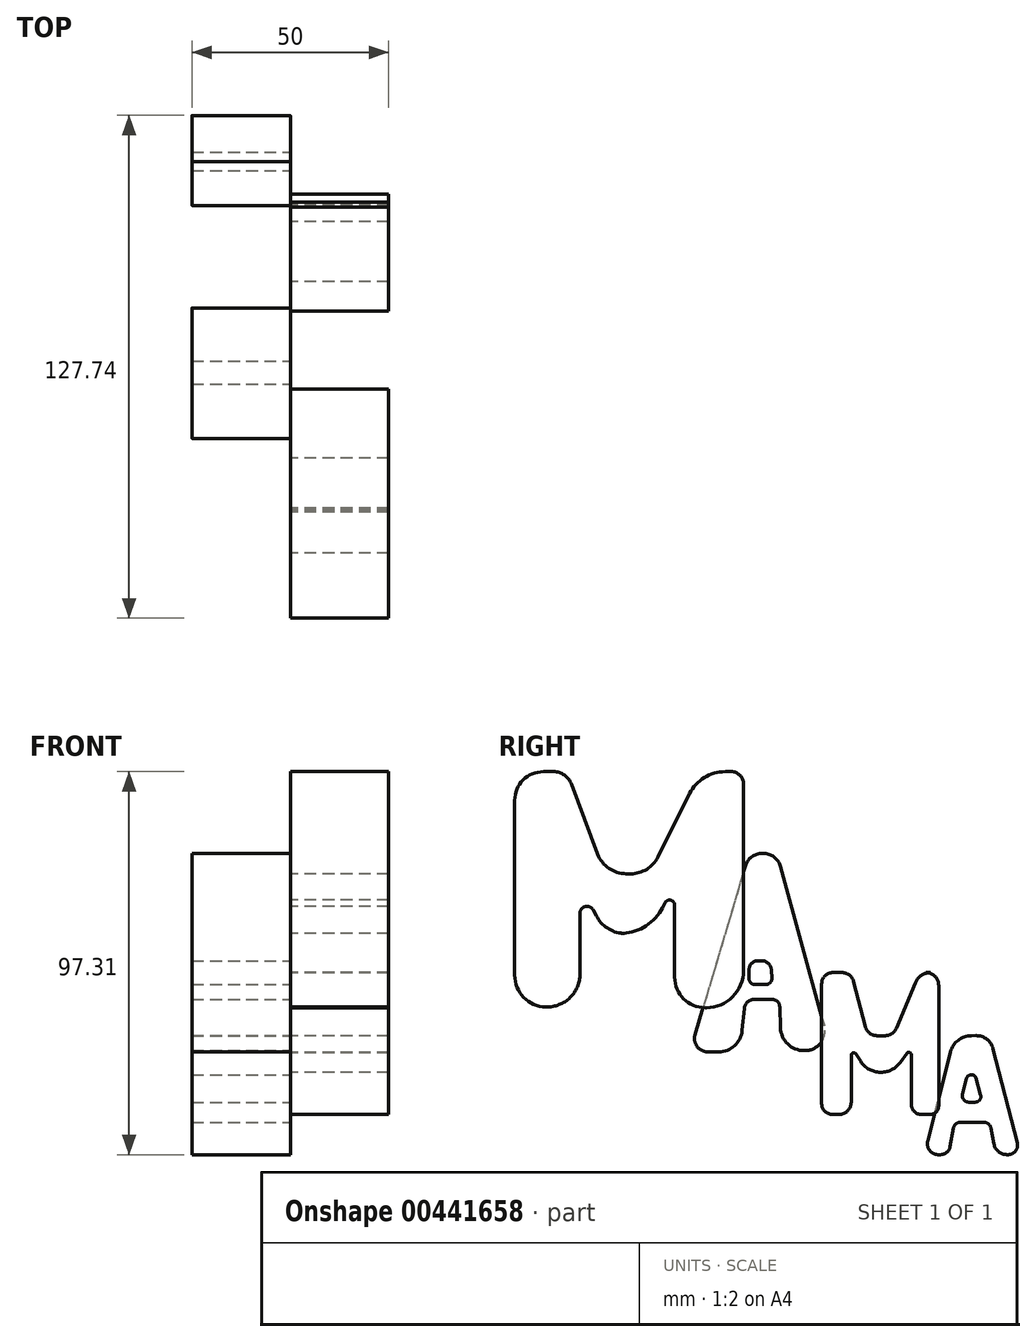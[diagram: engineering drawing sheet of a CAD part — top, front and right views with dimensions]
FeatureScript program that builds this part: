
annotation { "Feature Type Name" : "Feature", "Feature Type Description" : "" }
export const myFeature = defineFeature(function(context is Context, id is Id, definition is map)
    precondition{}
    {
        {
            var Q0;
            Q0=qCreatedBy(makeId("Right.planeOp"),FACE);
            var sketch = newSketch(context, id + "F0", { "sketchPlane" : qUnion([Q0])});
            skLineSegment(sketch, "E0", {"start": v(-70.27, 15.39) * mm, "end": v(-70.27, 59.77) * mm});
            skLineSegment(sketch, "E1", {"start": v(-62.96, 67.08) * mm, "end": v(-60.43, 67.08) * mm});
            skLineSegment(sketch, "E2", {"start": v(-55.84, 63.9) * mm, "end": v(-49.18, 46.14) * mm});
            skLineSegment(sketch, "E3", {"start": v(-41.96, 41.14) * mm, "end": v(-40.77, 41.14) * mm});
            skLineSegment(sketch, "E4", {"start": v(-33.87, 45.4) * mm, "end": v(-25.83, 61.5) * mm});
            skLineSegment(sketch, "E5", {"start": v(-16.78, 67.08) * mm, "end": v(-15.23, 67.08) * mm});
            skLineSegment(sketch, "E6", {"start": v(-12.12, 63.97) * mm, "end": v(-12.12, 16.58) * mm});
            skLineSegment(sketch, "E7", {"start": v(-21.6, 7.1) * mm, "end": v(-21.85, 7.1) * mm});
            skLineSegment(sketch, "E8", {"start": v(-29.62, 14.89) * mm, "end": v(-29.62, 33.15) * mm});
            skLineSegment(sketch, "E9", {"start": v(-32.1, 33.74) * mm, "end": v(-32.71, 32.52) * mm});
            skLineSegment(sketch, "E10", {"start": v(-42.31, 26) * mm, "end": v(-43.3, 26) * mm});
            skLineSegment(sketch, "E11", {"start": v(-49.56, 30.46) * mm, "end": v(-50.27, 31.88) * mm});
            skLineSegment(sketch, "E12", {"start": v(-53.68, 31.07) * mm, "end": v(-53.68, 15.69) * mm});
            skLineSegment(sketch, "E13", {"start": v(-62.26, 7.3) * mm, "end": v(-62.36, 7.3) * mm});
            skPoint(sketch, "E14.visualSharp", {"position": v(-70.27, 67.08) * mm});
            skArc(sketch, "E14.filletArc", {"start": v(-62.96, 67.08) * mm, "mid": v(-68.13, 64.94) * mm, "end": v(-70.27, 59.77) * mm});
            skPoint(sketch, "E15.visualSharp", {"position": v(-57.03, 67.08) * mm});
            skArc(sketch, "E15.filletArc", {"start": v(-55.84, 63.9) * mm, "mid": v(-57.64, 66.21) * mm, "end": v(-60.43, 67.08) * mm});
            skPoint(sketch, "E16.visualSharp", {"position": v(-23.03, 67.08) * mm});
            skArc(sketch, "E16.filletArc", {"start": v(-16.78, 67.08) * mm, "mid": v(-22.1, 65.57) * mm, "end": v(-25.83, 61.5) * mm});
            skPoint(sketch, "E17.visualSharp", {"position": v(-12.12, 67.08) * mm});
            skArc(sketch, "E17.filletArc", {"start": v(-12.12, 63.97) * mm, "mid": v(-13.03, 66.17) * mm, "end": v(-15.23, 67.08) * mm});
            skPoint(sketch, "E18.visualSharp", {"position": v(-12.12, 7.1) * mm});
            skArc(sketch, "E18.filletArc", {"start": v(-21.6, 7.1) * mm, "mid": v(-14.9, 9.88) * mm, "end": v(-12.12, 16.58) * mm});
            skPoint(sketch, "E19.visualSharp", {"position": v(-29.62, 7.1) * mm});
            skArc(sketch, "E19.filletArc", {"start": v(-29.62, 14.89) * mm, "mid": v(-27.34, 9.39) * mm, "end": v(-21.85, 7.1) * mm});
            skPoint(sketch, "E20.visualSharp", {"position": v(-70.27, 7.47) * mm});
            skArc(sketch, "E20.filletArc", {"start": v(-70.27, 15.39) * mm, "mid": v(-67.97, 9.73) * mm, "end": v(-62.36, 7.3) * mm});
            skPoint(sketch, "E21.visualSharp", {"position": v(-53.68, 7.1) * mm});
            skArc(sketch, "E21.filletArc", {"start": v(-62.26, 7.3) * mm, "mid": v(-56.2, 9.69) * mm, "end": v(-53.68, 15.69) * mm});
            skPoint(sketch, "E22.visualSharp", {"position": v(-47.3, 41.14) * mm});
            skArc(sketch, "E22.filletArc", {"start": v(-49.18, 46.14) * mm, "mid": v(-46.35, 42.5) * mm, "end": v(-41.96, 41.14) * mm});
            skPoint(sketch, "E23.visualSharp", {"position": v(-36, 41.14) * mm});
            skArc(sketch, "E23.filletArc", {"start": v(-40.77, 41.14) * mm, "mid": v(-36.71, 42.29) * mm, "end": v(-33.87, 45.4) * mm});
            skPoint(sketch, "E24.visualSharp", {"position": v(-29.62, 38.64) * mm});
            skArc(sketch, "E24.filletArc", {"start": v(-29.62, 33.15) * mm, "mid": v(-30.63, 34.42) * mm, "end": v(-32.1, 33.74) * mm});
            skPoint(sketch, "E25.visualSharp", {"position": v(-53.68, 38.64) * mm});
            skArc(sketch, "E25.filletArc", {"start": v(-50.27, 31.88) * mm, "mid": v(-52.3, 32.82) * mm, "end": v(-53.68, 31.07) * mm});
            skPoint(sketch, "E26.visualSharp", {"position": v(-47.3, 26) * mm});
            skArc(sketch, "E26.filletArc", {"start": v(-49.56, 30.46) * mm, "mid": v(-46.56, 27.21) * mm, "end": v(-42.31, 26) * mm});
            skPoint(sketch, "E27.visualSharp", {"position": v(-36, 26) * mm});
            skArc(sketch, "E27.filletArc", {"start": v(-43.3, 26) * mm, "mid": v(-37.08, 27.77) * mm, "end": v(-32.71, 32.52) * mm});
            skSolve(sketch);
        }
        {
            var Q0;
            Q0 = qSketchRegion(id + "F0", true);
            extrude(context, id + "F1", {"entities" : qUnion([Q0]), "depth" : 25 * mm});
        }
        {
            var Q0;
            Q0=qCreatedBy(makeId("Right.planeOp"),FACE);
            var sketch = newSketch(context, id + "F2", { "sketchPlane" : qUnion([Q0])});
            skLineSegment(sketch, "E28", {"start": v(-7.36, 46.33) * mm, "end": v(-7.12, 46.33) * mm});
            skLineSegment(sketch, "E29", {"start": v(-2.77, 43.01) * mm, "end": v(8.36, 2.57) * mm});
            skLineSegment(sketch, "E30", {"start": v(3.52, -3.8) * mm, "end": v(3.28, -3.8) * mm});
            skLineSegment(sketch, "E31", {"start": v(-18.45, -4.12) * mm, "end": v(-21.19, -4.12) * mm});
            skLineSegment(sketch, "E32", {"start": v(-11.7, 43.1) * mm, "end": v(-24.44, 0.24) * mm});
            skLineSegment(sketch, "E33", {"start": v(-10.73, 16.8) * mm, "end": v(-10.73, 14.5) * mm});
            skLineSegment(sketch, "E34", {"start": v(-8.48, 19.05) * mm, "end": v(-7.54, 19.05) * mm});
            skLineSegment(sketch, "E35", {"start": v(-9.24, 13.01) * mm, "end": v(-6.43, 13.01) * mm});
            skLineSegment(sketch, "E36", {"start": v(-4.94, 14.58) * mm, "end": v(-5.04, 16.67) * mm});
            skPoint(sketch, "E37.end.orphan", {"position": v(-3.68, 2.3) * mm});
            skPoint(sketch, "E38.end.orphan", {"position": v(-10.73, 10) * mm});
            skLineSegment(sketch, "E39", {"start": v(-9.36, 9.24) * mm, "end": v(-4.92, 9.24) * mm});
            skLineSegment(sketch, "E40", {"start": v(-2.93, 7.3) * mm, "end": v(-2.75, 2.03) * mm});
            skLineSegment(sketch, "E41", {"start": v(-11.95, 6.88) * mm, "end": v(-12.47, 1.32) * mm});
            skPoint(sketch, "E42.visualSharp", {"position": v(-10.73, 46.33) * mm});
            skArc(sketch, "E42.filletArc", {"start": v(-7.36, 46.33) * mm, "mid": v(-10.06, 45.44) * mm, "end": v(-11.7, 43.1) * mm});
            skPoint(sketch, "E43.visualSharp", {"position": v(-3.68, 46.33) * mm});
            skArc(sketch, "E43.filletArc", {"start": v(-2.77, 43.01) * mm, "mid": v(-4.39, 45.4) * mm, "end": v(-7.12, 46.33) * mm});
            skPoint(sketch, "E44.visualSharp", {"position": v(10.11, -3.8) * mm});
            skArc(sketch, "E44.filletArc", {"start": v(3.52, -3.8) * mm, "mid": v(7.51, -1.81) * mm, "end": v(8.36, 2.57) * mm});
            skPoint(sketch, "E45.visualSharp", {"position": v(-2.55, -3.8) * mm});
            skArc(sketch, "E45.filletArc", {"start": v(-2.75, 2.03) * mm, "mid": v(-0.91, -2.1) * mm, "end": v(3.28, -3.8) * mm});
            skPoint(sketch, "E46.visualSharp", {"position": v(-3, 9.24) * mm});
            skArc(sketch, "E46.filletArc", {"start": v(-2.93, 7.3) * mm, "mid": v(-3.53, 8.67) * mm, "end": v(-4.92, 9.24) * mm});
            skPoint(sketch, "E47.visualSharp", {"position": v(-11.73, 9.24) * mm});
            skArc(sketch, "E47.filletArc", {"start": v(-9.36, 9.24) * mm, "mid": v(-11.11, 8.56) * mm, "end": v(-11.95, 6.88) * mm});
            skPoint(sketch, "E48.visualSharp", {"position": v(-12.99, -4.12) * mm});
            skArc(sketch, "E48.filletArc", {"start": v(-18.45, -4.12) * mm, "mid": v(-14.4, -2.56) * mm, "end": v(-12.47, 1.32) * mm});
            skPoint(sketch, "E49.visualSharp", {"position": v(-25.74, -4.12) * mm});
            skArc(sketch, "E49.filletArc", {"start": v(-24.44, 0.24) * mm, "mid": v(-23.91, -2.76) * mm, "end": v(-21.19, -4.12) * mm});
            skPoint(sketch, "E50.visualSharp", {"position": v(-10.73, 19.05) * mm});
            skArc(sketch, "E50.filletArc", {"start": v(-8.48, 19.05) * mm, "mid": v(-10.07, 18.39) * mm, "end": v(-10.73, 16.8) * mm});
            skPoint(sketch, "E51.visualSharp", {"position": v(-5.16, 19.05) * mm});
            skArc(sketch, "E51.filletArc", {"start": v(-5.04, 16.67) * mm, "mid": v(-5.82, 18.36) * mm, "end": v(-7.54, 19.05) * mm});
            skPoint(sketch, "E52.visualSharp", {"position": v(-10.73, 13.01) * mm});
            skArc(sketch, "E52.filletArc", {"start": v(-10.73, 14.5) * mm, "mid": v(-10.3, 13.45) * mm, "end": v(-9.24, 13.01) * mm});
            skPoint(sketch, "E53.visualSharp", {"position": v(-4.86, 13.01) * mm});
            skArc(sketch, "E53.filletArc", {"start": v(-6.43, 13.01) * mm, "mid": v(-5.35, 13.48) * mm, "end": v(-4.94, 14.58) * mm});
            skSolve(sketch);
        }
        {
            var Q0;
            Q0 = qSketchRegion(id + "F2", true);
            extrude(context, id + "F3", {"entities" : qUnion([Q0]), "operationType" : NewBodyOperationType.ADD, "oppositeDirection" : true, "depth" : 25 * mm});
        }
        {
            var Q0;
            Q0=qCreatedBy(makeId("Right.planeOp"),FACE);
            var sketch = newSketch(context, id + "F4", { "sketchPlane" : qUnion([Q0])});
            skLineSegment(sketch, "E54", {"start": v(7.71, -17.27) * mm, "end": v(7.71, 13.13) * mm});
            skLineSegment(sketch, "E55", {"start": v(10.62, 16.04) * mm, "end": v(12.88, 16.04) * mm});
            skLineSegment(sketch, "E56", {"start": v(15.82, 13.77) * mm, "end": v(18.82, 2.27) * mm});
            skLineSegment(sketch, "E57", {"start": v(21.76, 0) * mm, "end": v(23.89, 0) * mm});
            skLineSegment(sketch, "E58", {"start": v(26.7, 1.87) * mm, "end": v(31.52, 13.47) * mm});
            skLineSegment(sketch, "E59", {"start": v(34.19, 16.04) * mm, "end": v(35.37, 16.04) * mm});
            skLineSegment(sketch, "E60", {"start": v(37.45, 12.78) * mm, "end": v(37.45, -17.82) * mm});
            skLineSegment(sketch, "E61", {"start": v(10.45, -20.01) * mm, "end": v(12.1, -20.01) * mm});
            skLineSegment(sketch, "E62", {"start": v(15.23, -16.9) * mm, "end": v(15.23, -4.96) * mm});
            skLineSegment(sketch, "E63", {"start": v(16.38, -4.61) * mm, "end": v(17.64, -6.56) * mm});
            skLineSegment(sketch, "E64", {"start": v(22.67, -9.29) * mm, "end": v(22.82, -9.29) * mm});
            skLineSegment(sketch, "E65", {"start": v(27.7, -6.76) * mm, "end": v(29.33, -4.47) * mm});
            skLineSegment(sketch, "E66", {"start": v(30.48, -4.83) * mm, "end": v(30.48, -17.42) * mm});
            skLineSegment(sketch, "E67", {"start": v(33.07, -20.01) * mm, "end": v(35.26, -20.01) * mm});
            skPoint(sketch, "E68.visualSharp", {"position": v(7.71, 16.04) * mm});
            skArc(sketch, "E68.filletArc", {"start": v(10.62, 16.04) * mm, "mid": v(8.57, 15.19) * mm, "end": v(7.71, 13.13) * mm});
            skPoint(sketch, "E69.visualSharp", {"position": v(15.23, 16.04) * mm});
            skArc(sketch, "E69.filletArc", {"start": v(15.82, 13.77) * mm, "mid": v(14.74, 15.4) * mm, "end": v(12.88, 16.04) * mm});
            skPoint(sketch, "E70.visualSharp", {"position": v(19.42, 0) * mm});
            skArc(sketch, "E70.filletArc", {"start": v(18.82, 2.27) * mm, "mid": v(19.9, 0.63) * mm, "end": v(21.76, 0) * mm});
            skPoint(sketch, "E71.visualSharp", {"position": v(25.91, 0) * mm});
            skArc(sketch, "E71.filletArc", {"start": v(23.89, 0) * mm, "mid": v(25.57, 0.5) * mm, "end": v(26.7, 1.87) * mm});
            skPoint(sketch, "E72.visualSharp", {"position": v(32.6, 16.04) * mm});
            skArc(sketch, "E72.filletArc", {"start": v(35.37, 16.04) * mm, "mid": v(33.06, 15.34) * mm, "end": v(31.52, 13.47) * mm});
            skPoint(sketch, "E73.visualSharp", {"position": v(37.45, 16.04) * mm});
            skArc(sketch, "E73.filletArc", {"start": v(37.45, 12.78) * mm, "mid": v(36.5, 15.08) * mm, "end": v(34.19, 16.04) * mm});
            skPoint(sketch, "E74.visualSharp", {"position": v(37.45, -20.01) * mm});
            skArc(sketch, "E74.filletArc", {"start": v(35.26, -20.01) * mm, "mid": v(36.81, -19.37) * mm, "end": v(37.45, -17.82) * mm});
            skPoint(sketch, "E75.visualSharp", {"position": v(30.48, -20.01) * mm});
            skArc(sketch, "E75.filletArc", {"start": v(30.48, -17.42) * mm, "mid": v(31.24, -19.25) * mm, "end": v(33.07, -20.01) * mm});
            skPoint(sketch, "E76.visualSharp", {"position": v(15.23, -20.01) * mm});
            skArc(sketch, "E76.filletArc", {"start": v(12.1, -20.01) * mm, "mid": v(14.31, -19.1) * mm, "end": v(15.23, -16.9) * mm});
            skPoint(sketch, "E77.visualSharp", {"position": v(7.71, -20.01) * mm});
            skArc(sketch, "E77.filletArc", {"start": v(7.71, -17.27) * mm, "mid": v(8.51, -19.21) * mm, "end": v(10.45, -20.01) * mm});
            skPoint(sketch, "E78.visualSharp", {"position": v(15.23, -2.85) * mm});
            skArc(sketch, "E78.filletArc", {"start": v(16.38, -4.61) * mm, "mid": v(15.67, -4.36) * mm, "end": v(15.23, -4.96) * mm});
            skPoint(sketch, "E79.visualSharp", {"position": v(30.48, -2.85) * mm});
            skArc(sketch, "E79.filletArc", {"start": v(30.48, -4.83) * mm, "mid": v(30.04, -4.23) * mm, "end": v(29.33, -4.47) * mm});
            skPoint(sketch, "E80.visualSharp", {"position": v(19.42, -9.29) * mm});
            skArc(sketch, "E80.filletArc", {"start": v(17.64, -6.56) * mm, "mid": v(19.8, -8.56) * mm, "end": v(22.67, -9.29) * mm});
            skPoint(sketch, "E81.visualSharp", {"position": v(25.91, -9.29) * mm});
            skArc(sketch, "E81.filletArc", {"start": v(22.82, -9.29) * mm, "mid": v(25.57, -8.62) * mm, "end": v(27.7, -6.76) * mm});
            skSolve(sketch);
        }
        {
            var Q0;
            Q0 = qSketchRegion(id + "F4", true);
            extrude(context, id + "F5", {"entities" : qUnion([Q0]), "operationType" : NewBodyOperationType.ADD, "depth" : 25 * mm});
        }
        {
            var Q0;
            Q0=qCreatedBy(makeId("Right.planeOp"),FACE);
            var sketch = newSketch(context, id + "F6", { "sketchPlane" : qUnion([Q0])});
            skLineSegment(sketch, "E82", {"start": v(34.66, -26.78) * mm, "end": v(40.47, -4.1) * mm});
            skLineSegment(sketch, "E83", {"start": v(51.27, -3.3) * mm, "end": v(57.4, -27.25) * mm});
            skLineSegment(sketch, "E84", {"start": v(55.08, -30.23) * mm, "end": v(54.8, -30.23) * mm});
            skLineSegment(sketch, "E85", {"start": v(37.34, -30.23) * mm, "end": v(37.95, -30.23) * mm});
            skLineSegment(sketch, "E86", {"start": v(40.3, -28.3) * mm, "end": v(41.26, -23.4) * mm});
            skLineSegment(sketch, "E87", {"start": v(42.91, -22.03) * mm, "end": v(49.01, -22.03) * mm});
            skLineSegment(sketch, "E88", {"start": v(50.68, -23.4) * mm, "end": v(51.49, -27.5) * mm});
            skLineSegment(sketch, "E89", {"start": v(43.5, -14.86) * mm, "end": v(44.54, -10.82) * mm});
            skLineSegment(sketch, "E90", {"start": v(45.64, -9.97) * mm, "end": v(45.94, -9.97) * mm});
            skLineSegment(sketch, "E91", {"start": v(45.09, -16.9) * mm, "end": v(46.7, -16.9) * mm});
            skLineSegment(sketch, "E92", {"start": v(48.1, -15.05) * mm, "end": v(46.9, -10.7) * mm});
            skPoint(sketch, "E93.visualSharp", {"position": v(41.52, 0) * mm});
            skArc(sketch, "E93.filletArc", {"start": v(45.75, 0) * mm, "mid": v(42.41, -1.14) * mm, "end": v(40.47, -4.1) * mm});
            skPoint(sketch, "E94.visualSharp", {"position": v(44.76, -9.97) * mm});
            skArc(sketch, "E94.filletArc", {"start": v(45.64, -9.97) * mm, "mid": v(44.94, -10.2) * mm, "end": v(44.54, -10.82) * mm});
            skPoint(sketch, "E95.visualSharp", {"position": v(46.69, -9.97) * mm});
            skArc(sketch, "E95.filletArc", {"start": v(46.9, -10.7) * mm, "mid": v(46.54, -10.17) * mm, "end": v(45.94, -9.97) * mm});
            skPoint(sketch, "E96.visualSharp", {"position": v(48.62, -16.9) * mm});
            skArc(sketch, "E96.filletArc", {"start": v(46.7, -16.9) * mm, "mid": v(47.86, -16.32) * mm, "end": v(48.1, -15.05) * mm});
            skPoint(sketch, "E97.visualSharp", {"position": v(42.99, -16.9) * mm});
            skArc(sketch, "E97.filletArc", {"start": v(43.5, -14.86) * mm, "mid": v(43.8, -16.26) * mm, "end": v(45.09, -16.9) * mm});
            skPoint(sketch, "E98.visualSharp", {"position": v(52.02, -30.23) * mm});
            skArc(sketch, "E98.filletArc", {"start": v(51.49, -27.5) * mm, "mid": v(52.65, -29.46) * mm, "end": v(54.8, -30.23) * mm});
            skPoint(sketch, "E99.visualSharp", {"position": v(58.15, -30.23) * mm});
            skArc(sketch, "E99.filletArc", {"start": v(55.08, -30.23) * mm, "mid": v(56.97, -29.3) * mm, "end": v(57.4, -27.25) * mm});
            skPoint(sketch, "E100.visualSharp", {"position": v(39.91, -30.23) * mm});
            skArc(sketch, "E100.filletArc", {"start": v(37.95, -30.23) * mm, "mid": v(39.47, -29.68) * mm, "end": v(40.3, -28.3) * mm});
            skPoint(sketch, "E101.visualSharp", {"position": v(33.78, -30.23) * mm});
            skArc(sketch, "E101.filletArc", {"start": v(34.66, -26.78) * mm, "mid": v(35.16, -29.16) * mm, "end": v(37.34, -30.23) * mm});
            skPoint(sketch, "E102.visualSharp", {"position": v(41.52, -22.03) * mm});
            skArc(sketch, "E102.filletArc", {"start": v(42.91, -22.03) * mm, "mid": v(41.84, -22.41) * mm, "end": v(41.26, -23.4) * mm});
            skPoint(sketch, "E103.visualSharp", {"position": v(50.41, -22.03) * mm});
            skArc(sketch, "E103.filletArc", {"start": v(50.68, -23.4) * mm, "mid": v(50.1, -22.41) * mm, "end": v(49.01, -22.03) * mm});
            skLineSegment(sketch, "E104", {"start": v(45.75, 0) * mm, "end": v(46.95, 0.01) * mm});
            skPoint(sketch, "E105.visualSharp", {"position": v(50.41, 0.05) * mm});
            skArc(sketch, "E105.filletArc", {"start": v(51.27, -3.3) * mm, "mid": v(49.68, -0.9) * mm, "end": v(46.95, 0.01) * mm});
            skSolve(sketch);
        }
        {
            var Q0;
            Q0 = qSketchRegion(id + "F6", true);
            extrude(context, id + "F7", {"entities" : qUnion([Q0]), "operationType" : NewBodyOperationType.ADD, "oppositeDirection" : true, "depth" : 25 * mm});
        }
    });
